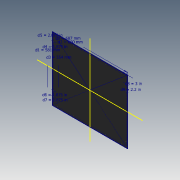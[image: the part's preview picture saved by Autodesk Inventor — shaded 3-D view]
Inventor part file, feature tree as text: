
AUTODESK INVENTOR PART (.ipt)
format: ipt  version: 2020.3 (Build 243373000, 373)  size: 145,920 bytes
history: native  units: in
note: dims shown in document units (in); Inventor stores cm internally (conversion verified against a paired STEP export)
features: sketch x2, hole x2, extrude x1, fillet x1
ambient origin geometry x8: Origin, YZ Plane, XZ Plane, XY Plane, X Axis, Y Axis, Z Axis, Center Point
bodies: Solid1 (feature_tree)
feature tree (6):
  sketch  "Sketch1"  dims[d0=27.0472in d1=22.874in]
  extrude  "Extrusion1"  Depth=22.874in
  hole  "Hole1"  [1 undecoded]
  hole  "Hole2"  [1 undecoded]
  fillet  "Fillet1"  Radius=2.875in
  sketch  "Sketch2"  dims[d2=25.9843in d3=21.811in d4=1.875in d5=2.875in d6=1.875in d7=2.875in d8=3.0in d9=2.2in d10=0.125in d11=0.0in d12=0.24in d13=0.75in d14=0.375in d15=0.25in d16=0.5635in d17=1.0in d18=0.8108in d19=5.75in d20=5.75in d21=5.75in d22=5.75in d23=4.75in d24=4.75in d25=4.75in d26=4.75in d27=0.18in d28=0.75in d29=0.375in d30=0.25in d31=0.5635in d32=1.0in d33=0.8108in d34=0.1875in]
note: 2 required parameter values undecoded (feature->parameter linkage not recoverable at this tier; creation-order binding heuristic only, values carry confidence <= 0.55)
